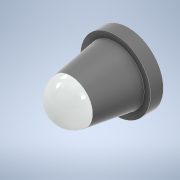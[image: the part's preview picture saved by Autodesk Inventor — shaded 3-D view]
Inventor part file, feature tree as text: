
AUTODESK INVENTOR PART (.ipt)
format: ipt  version: 2021 (Build 250183000, 183)  size: 135,680 bytes
history: native  units: mm
features: sketch x3, other x2, extrude x1, loft x1, fillet x1
ambient origin geometry x8: Origin, YZ Plane, XZ Plane, XY Plane, X Axis, Y Axis, Z Axis, Center Point
bodies: Body1 (feature_tree)
feature tree (8):
  other  "Sólido1"
  extrude  "Extrusão1"  Depth=20.0mm TaperAngle=0.0deg
  sketch  "Esboço2"  dims[d3=89.9mm d5=100.0mm d6=60.0mm]
  other  "Plano de trabalho2"
  loft  "Transição1"
  fillet  "Arredondamento1"  Radius=60.0mm
  sketch  "Esboço1"  dims[d0=110.0mm d1=20.0mm d2=0.0mm]
  sketch  "Esboço3"  dims[d7=0.0mm d8=90.0deg d9=0.0mm d10=90.0deg d11=34.8mm]
